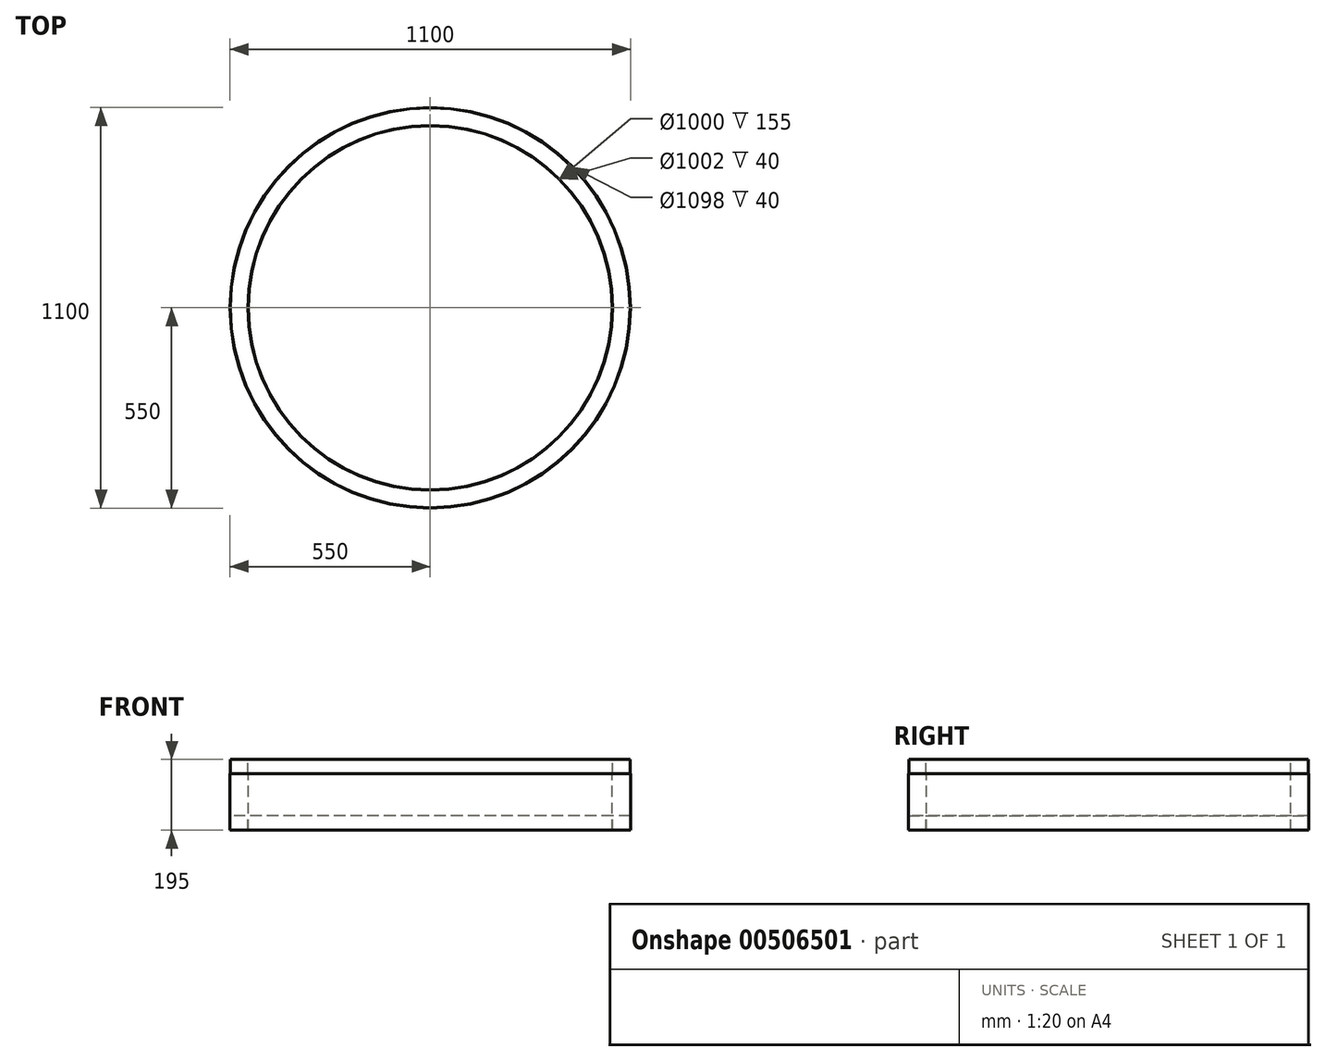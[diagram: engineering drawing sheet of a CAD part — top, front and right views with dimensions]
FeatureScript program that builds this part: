
annotation { "Feature Type Name" : "Feature", "Feature Type Description" : "" }
export const myFeature = defineFeature(function(context is Context, id is Id, definition is map)
    precondition{}
    {
        {
            var Q0;
            Q0=qCreatedBy(makeId("Front.planeOp"),FACE);
            var sketch = newSketch(context, id + "F0", { "sketchPlane" : qUnion([Q0])});
            skLineSegment(sketch, "E0", {"start": v(0, 74.87) * mm, "end": v(0, -73.71) * mm, "construction": true});
            skLineSegment(sketch, "E1", {"start": v(0, 374.84) * mm, "end": v(0, -528.94) * mm, "construction": true});
            skLineSegment(sketch, "E2", {"start": v(-500, -489.75) * mm, "end": v(-500, -334.75) * mm});
            skLineSegment(sketch, "E3", {"start": v(-500, -334.75) * mm, "end": v(-501, -334.75) * mm});
            skLineSegment(sketch, "E4", {"start": v(-501, -334.75) * mm, "end": v(-501, -294.75) * mm});
            skLineSegment(sketch, "E5", {"start": v(-501, -294.75) * mm, "end": v(-549, -294.75) * mm});
            skLineSegment(sketch, "E6", {"start": v(-549, -294.75) * mm, "end": v(-549, -334.75) * mm});
            skLineSegment(sketch, "E7", {"start": v(-549, -334.75) * mm, "end": v(-550, -334.75) * mm});
            skLineSegment(sketch, "E8", {"start": v(-550, -334.75) * mm, "end": v(-550, -489.75) * mm});
            skLineSegment(sketch, "E9", {"start": v(-550, -489.75) * mm, "end": v(-549, -489.75) * mm});
            skLineSegment(sketch, "E10", {"start": v(-549, -489.75) * mm, "end": v(-549, -449.75) * mm});
            skLineSegment(sketch, "E11", {"start": v(-549, -449.75) * mm, "end": v(-501, -449.75) * mm});
            skLineSegment(sketch, "E12", {"start": v(-501, -449.75) * mm, "end": v(-501, -489.75) * mm});
            skLineSegment(sketch, "E13", {"start": v(-501, -489.75) * mm, "end": v(-500, -489.75) * mm});
            skSolve(sketch);
        }
        {
            var Q0;
            Q0=qSketchRegion(id+"F0",true);
            var Q1;
            Q1=sQuery(id+"F0.wireOp",EDGE,"E1");
            revolve(context, id + "F1", {"entities" : qUnion([Q0]), "axis" : qUnion([Q1]), "revolveType" : RevolveType.FULL});
        }
    });
